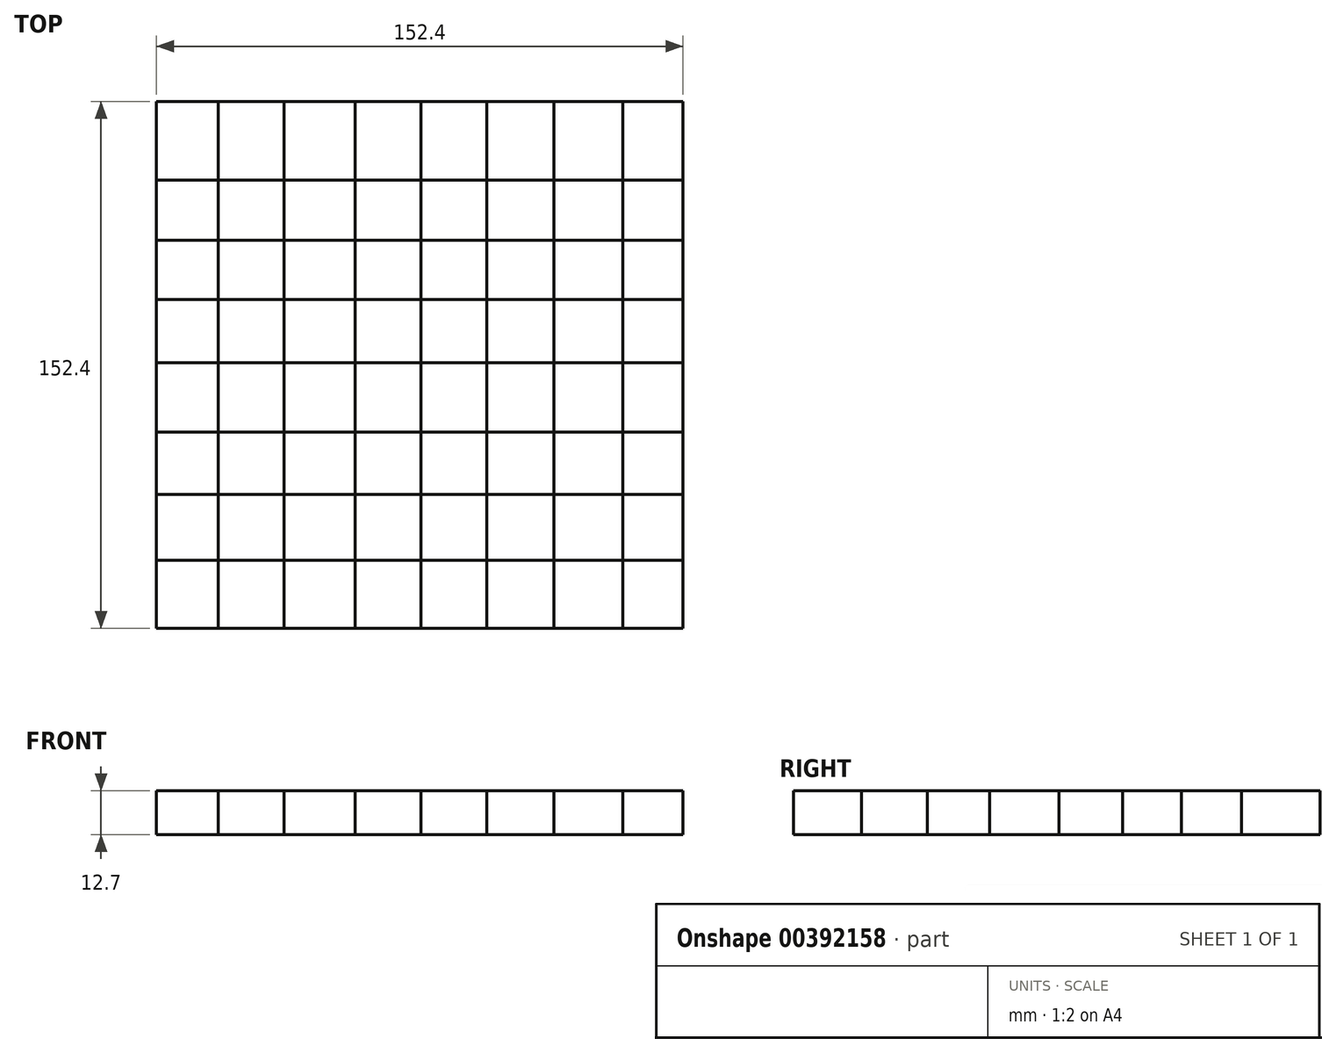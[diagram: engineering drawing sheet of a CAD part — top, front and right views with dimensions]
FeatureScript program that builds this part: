
annotation { "Feature Type Name" : "Feature", "Feature Type Description" : "" }
export const myFeature = defineFeature(function(context is Context, id is Id, definition is map)
    precondition{}
    {
        {
            var Q0;
            Q0=qCreatedBy(makeId("Top.planeOp"),FACE);
            var sketch = newSketch(context, id + "F0", { "sketchPlane" : qUnion([Q0])});
            skLineSegment(sketch, "E0.bottom", {"start": v(-76.58, 75.62) * mm, "end": v(75.82, 75.62) * mm});
            skLineSegment(sketch, "E0.top", {"start": v(-76.58, -76.78) * mm, "end": v(75.82, -76.78) * mm});
            skLineSegment(sketch, "E0.left", {"start": v(-76.58, 75.62) * mm, "end": v(-76.58, -76.78) * mm});
            skLineSegment(sketch, "E0.right", {"start": v(75.82, 75.62) * mm, "end": v(75.82, -76.78) * mm});
            skLineSegment(sketch, "E1", {"start": v(-58.72, 75.62) * mm, "end": v(-58.72, -76.78) * mm});
            skLineSegment(sketch, "E2", {"start": v(-39.68, 75.62) * mm, "end": v(-39.68, -76.78) * mm});
            skLineSegment(sketch, "E3", {"start": v(-19.03, 75.62) * mm, "end": v(-19.03, -76.78) * mm});
            skLineSegment(sketch, "E4", {"start": v(0, 75.62) * mm, "end": v(0, -76.78) * mm});
            skLineSegment(sketch, "E5", {"start": v(19.03, 75.62) * mm, "end": v(19.03, -76.78) * mm});
            skLineSegment(sketch, "E6", {"start": v(38.4, 75.62) * mm, "end": v(38.4, -76.78) * mm});
            skLineSegment(sketch, "E7", {"start": v(58.4, 75.62) * mm, "end": v(58.4, -76.78) * mm});
            skLineSegment(sketch, "E8", {"start": v(-76.58, -57.1) * mm, "end": v(75.82, -57.1) * mm});
            skLineSegment(sketch, "E9", {"start": v(-76.58, -38.07) * mm, "end": v(75.82, -38.07) * mm});
            skLineSegment(sketch, "E10", {"start": v(-76.58, -20) * mm, "end": v(75.82, -20) * mm});
            skLineSegment(sketch, "E11", {"start": v(-76.58, 0) * mm, "end": v(75.82, 0) * mm});
            skLineSegment(sketch, "E12", {"start": v(-76.58, 18.39) * mm, "end": v(75.82, 18.39) * mm});
            skLineSegment(sketch, "E13", {"start": v(-76.58, 35.49) * mm, "end": v(75.82, 35.49) * mm});
            skLineSegment(sketch, "E14", {"start": v(-76.58, 52.9) * mm, "end": v(75.82, 52.9) * mm});
            skSolve(sketch);
        }
        {
            var Q0;
            {var subQ0=sQuery(id+"F0.wireOp",EDGE,"E0.left");var subQ1=sQuery(id+"F0.wireOp",EDGE,"E0.bottom");var subQ2=makeQuery(id+"F0.imprint","INTERSECT",VERTEX,{"derivedFrom":[subQ1,subQ0]});Q0=makeQuery(id+"F0.imprint","IMPRINT",FACE,{"disambiguationData":[TD([[makeQuery(id+"F0.imprint","IMPRINT",EDGE,{"disambiguationData":[TD([[subQ2,-1.0]])],"derivedFrom":subQ1}),-1.0]])]});}
            var Q1;
            {var subQ0=sQuery(id+"F0.wireOp",EDGE,"E2");var subQ1=sQuery(id+"F0.wireOp",EDGE,"E0.bottom");var subQ2=makeQuery(id+"F0.imprint","INTERSECT",VERTEX,{"derivedFrom":[subQ1,subQ0]});Q1=makeQuery(id+"F0.imprint","IMPRINT",FACE,{"disambiguationData":[TD([[makeQuery(id+"F0.imprint","IMPRINT",EDGE,{"disambiguationData":[TD([[subQ2,-1.0]])],"derivedFrom":subQ1}),-1.0]])]});}
            var Q2;
            {var subQ0=sQuery(id+"F0.wireOp",EDGE,"E4");var subQ1=sQuery(id+"F0.wireOp",EDGE,"E0.bottom");var subQ2=makeQuery(id+"F0.imprint","INTERSECT",VERTEX,{"derivedFrom":[subQ1,subQ0]});Q2=makeQuery(id+"F0.imprint","IMPRINT",FACE,{"disambiguationData":[TD([[makeQuery(id+"F0.imprint","IMPRINT",EDGE,{"disambiguationData":[TD([[subQ2,-1.0]])],"derivedFrom":subQ1}),-1.0]])]});}
            var Q3;
            {var subQ0=sQuery(id+"F0.wireOp",EDGE,"E6");var subQ1=sQuery(id+"F0.wireOp",EDGE,"E0.bottom");var subQ2=makeQuery(id+"F0.imprint","INTERSECT",VERTEX,{"derivedFrom":[subQ1,subQ0]});Q3=makeQuery(id+"F0.imprint","IMPRINT",FACE,{"disambiguationData":[TD([[makeQuery(id+"F0.imprint","IMPRINT",EDGE,{"disambiguationData":[TD([[subQ2,-1.0]])],"derivedFrom":subQ1}),-1.0]])]});}
            var Q4;
            {var subQ0=sQuery(id+"F0.wireOp",EDGE,"E14");var subQ1=sQuery(id+"F0.wireOp",EDGE,"E1");var subQ2=makeQuery(id+"F0.imprint","INTERSECT",VERTEX,{"derivedFrom":[subQ1,subQ0]});Q4=makeQuery(id+"F0.imprint","IMPRINT",FACE,{"disambiguationData":[TD([[makeQuery(id+"F0.imprint","IMPRINT",EDGE,{"disambiguationData":[TD([[subQ2,-1.0]])],"derivedFrom":subQ1}),1.0]])]});}
            var Q5;
            {var subQ0=sQuery(id+"F0.wireOp",EDGE,"E14");var subQ1=sQuery(id+"F0.wireOp",EDGE,"E3");var subQ2=makeQuery(id+"F0.imprint","INTERSECT",VERTEX,{"derivedFrom":[subQ1,subQ0]});Q5=makeQuery(id+"F0.imprint","IMPRINT",FACE,{"disambiguationData":[TD([[makeQuery(id+"F0.imprint","IMPRINT",EDGE,{"disambiguationData":[TD([[subQ2,-1.0]])],"derivedFrom":subQ1}),1.0]])]});}
            var Q6;
            {var subQ0=sQuery(id+"F0.wireOp",EDGE,"E14");var subQ1=sQuery(id+"F0.wireOp",EDGE,"E5");var subQ2=makeQuery(id+"F0.imprint","INTERSECT",VERTEX,{"derivedFrom":[subQ1,subQ0]});Q6=makeQuery(id+"F0.imprint","IMPRINT",FACE,{"disambiguationData":[TD([[makeQuery(id+"F0.imprint","IMPRINT",EDGE,{"disambiguationData":[TD([[subQ2,-1.0]])],"derivedFrom":subQ1}),1.0]])]});}
            var Q7;
            {var subQ0=sQuery(id+"F0.wireOp",EDGE,"E13");var subQ1=sQuery(id+"F0.wireOp",EDGE,"E0.right");var subQ2=makeQuery(id+"F0.imprint","INTERSECT",VERTEX,{"derivedFrom":[subQ1,subQ0]});Q7=makeQuery(id+"F0.imprint","IMPRINT",FACE,{"disambiguationData":[TD([[makeQuery(id+"F0.imprint","IMPRINT",EDGE,{"disambiguationData":[TD([[subQ2,1.0]])],"derivedFrom":subQ1}),-1.0]])]});}
            var Q8;
            {var subQ0=sQuery(id+"F0.wireOp",EDGE,"E13");var subQ1=sQuery(id+"F0.wireOp",EDGE,"E6");var subQ2=makeQuery(id+"F0.imprint","INTERSECT",VERTEX,{"derivedFrom":[subQ1,subQ0]});Q8=makeQuery(id+"F0.imprint","IMPRINT",FACE,{"disambiguationData":[TD([[makeQuery(id+"F0.imprint","IMPRINT",EDGE,{"disambiguationData":[TD([[subQ2,-1.0]])],"derivedFrom":subQ1}),1.0]])]});}
            var Q9;
            {var subQ0=sQuery(id+"F0.wireOp",EDGE,"E13");var subQ1=sQuery(id+"F0.wireOp",EDGE,"E4");var subQ2=makeQuery(id+"F0.imprint","INTERSECT",VERTEX,{"derivedFrom":[subQ1,subQ0]});Q9=makeQuery(id+"F0.imprint","IMPRINT",FACE,{"disambiguationData":[TD([[makeQuery(id+"F0.imprint","IMPRINT",EDGE,{"disambiguationData":[TD([[subQ2,-1.0]])],"derivedFrom":subQ1}),1.0]])]});}
            var Q10;
            {var subQ0=sQuery(id+"F0.wireOp",EDGE,"E13");var subQ1=sQuery(id+"F0.wireOp",EDGE,"E2");var subQ2=makeQuery(id+"F0.imprint","INTERSECT",VERTEX,{"derivedFrom":[subQ1,subQ0]});Q10=makeQuery(id+"F0.imprint","IMPRINT",FACE,{"disambiguationData":[TD([[makeQuery(id+"F0.imprint","IMPRINT",EDGE,{"disambiguationData":[TD([[subQ2,-1.0]])],"derivedFrom":subQ1}),1.0]])]});}
            var Q11;
            {var subQ0=sQuery(id+"F0.wireOp",EDGE,"E12");var subQ1=sQuery(id+"F0.wireOp",EDGE,"E0.left");var subQ2=makeQuery(id+"F0.imprint","INTERSECT",VERTEX,{"derivedFrom":[subQ1,subQ0]});Q11=makeQuery(id+"F0.imprint","IMPRINT",FACE,{"disambiguationData":[TD([[makeQuery(id+"F0.imprint","IMPRINT",EDGE,{"disambiguationData":[TD([[subQ2,1.0]])],"derivedFrom":subQ1}),1.0]])]});}
            var Q12;
            {var subQ0=sQuery(id+"F0.wireOp",EDGE,"E12");var subQ1=sQuery(id+"F0.wireOp",EDGE,"E1");var subQ2=makeQuery(id+"F0.imprint","INTERSECT",VERTEX,{"derivedFrom":[subQ1,subQ0]});Q12=makeQuery(id+"F0.imprint","IMPRINT",FACE,{"disambiguationData":[TD([[makeQuery(id+"F0.imprint","IMPRINT",EDGE,{"disambiguationData":[TD([[subQ2,-1.0]])],"derivedFrom":subQ1}),1.0]])]});}
            var Q13;
            {var subQ0=sQuery(id+"F0.wireOp",EDGE,"E12");var subQ1=sQuery(id+"F0.wireOp",EDGE,"E3");var subQ2=makeQuery(id+"F0.imprint","INTERSECT",VERTEX,{"derivedFrom":[subQ1,subQ0]});Q13=makeQuery(id+"F0.imprint","IMPRINT",FACE,{"disambiguationData":[TD([[makeQuery(id+"F0.imprint","IMPRINT",EDGE,{"disambiguationData":[TD([[subQ2,-1.0]])],"derivedFrom":subQ1}),1.0]])]});}
            var Q14;
            {var subQ0=sQuery(id+"F0.wireOp",EDGE,"E12");var subQ1=sQuery(id+"F0.wireOp",EDGE,"E5");var subQ2=makeQuery(id+"F0.imprint","INTERSECT",VERTEX,{"derivedFrom":[subQ1,subQ0]});Q14=makeQuery(id+"F0.imprint","IMPRINT",FACE,{"disambiguationData":[TD([[makeQuery(id+"F0.imprint","IMPRINT",EDGE,{"disambiguationData":[TD([[subQ2,-1.0]])],"derivedFrom":subQ1}),1.0]])]});}
            var Q15;
            {var subQ0=sQuery(id+"F0.wireOp",EDGE,"E11");var subQ1=sQuery(id+"F0.wireOp",EDGE,"E0.right");var subQ2=makeQuery(id+"F0.imprint","INTERSECT",VERTEX,{"derivedFrom":[subQ1,subQ0]});Q15=makeQuery(id+"F0.imprint","IMPRINT",FACE,{"disambiguationData":[TD([[makeQuery(id+"F0.imprint","IMPRINT",EDGE,{"disambiguationData":[TD([[subQ2,1.0]])],"derivedFrom":subQ1}),-1.0]])]});}
            var Q16;
            {var subQ0=sQuery(id+"F0.wireOp",EDGE,"E11");var subQ1=sQuery(id+"F0.wireOp",EDGE,"E6");var subQ2=makeQuery(id+"F0.imprint","INTERSECT",VERTEX,{"derivedFrom":[subQ1,subQ0]});Q16=makeQuery(id+"F0.imprint","IMPRINT",FACE,{"disambiguationData":[TD([[makeQuery(id+"F0.imprint","IMPRINT",EDGE,{"disambiguationData":[TD([[subQ2,-1.0]])],"derivedFrom":subQ1}),1.0]])]});}
            var Q17;
            {var subQ0=sQuery(id+"F0.wireOp",EDGE,"E11");var subQ1=sQuery(id+"F0.wireOp",EDGE,"E4");var subQ2=makeQuery(id+"F0.imprint","INTERSECT",VERTEX,{"derivedFrom":[subQ1,subQ0]});Q17=makeQuery(id+"F0.imprint","IMPRINT",FACE,{"disambiguationData":[TD([[makeQuery(id+"F0.imprint","IMPRINT",EDGE,{"disambiguationData":[TD([[subQ2,-1.0]])],"derivedFrom":subQ1}),1.0]])]});}
            var Q18;
            {var subQ0=sQuery(id+"F0.wireOp",EDGE,"E11");var subQ1=sQuery(id+"F0.wireOp",EDGE,"E2");var subQ2=makeQuery(id+"F0.imprint","INTERSECT",VERTEX,{"derivedFrom":[subQ1,subQ0]});Q18=makeQuery(id+"F0.imprint","IMPRINT",FACE,{"disambiguationData":[TD([[makeQuery(id+"F0.imprint","IMPRINT",EDGE,{"disambiguationData":[TD([[subQ2,-1.0]])],"derivedFrom":subQ1}),1.0]])]});}
            var Q19;
            {var subQ0=sQuery(id+"F0.wireOp",EDGE,"E10");var subQ1=sQuery(id+"F0.wireOp",EDGE,"E0.left");var subQ2=makeQuery(id+"F0.imprint","INTERSECT",VERTEX,{"derivedFrom":[subQ1,subQ0]});Q19=makeQuery(id+"F0.imprint","IMPRINT",FACE,{"disambiguationData":[TD([[makeQuery(id+"F0.imprint","IMPRINT",EDGE,{"disambiguationData":[TD([[subQ2,1.0]])],"derivedFrom":subQ1}),1.0]])]});}
            var Q20;
            {var subQ0=sQuery(id+"F0.wireOp",EDGE,"E10");var subQ1=sQuery(id+"F0.wireOp",EDGE,"E1");var subQ2=makeQuery(id+"F0.imprint","INTERSECT",VERTEX,{"derivedFrom":[subQ1,subQ0]});Q20=makeQuery(id+"F0.imprint","IMPRINT",FACE,{"disambiguationData":[TD([[makeQuery(id+"F0.imprint","IMPRINT",EDGE,{"disambiguationData":[TD([[subQ2,-1.0]])],"derivedFrom":subQ1}),1.0]])]});}
            var Q21;
            {var subQ0=sQuery(id+"F0.wireOp",EDGE,"E10");var subQ1=sQuery(id+"F0.wireOp",EDGE,"E3");var subQ2=makeQuery(id+"F0.imprint","INTERSECT",VERTEX,{"derivedFrom":[subQ1,subQ0]});Q21=makeQuery(id+"F0.imprint","IMPRINT",FACE,{"disambiguationData":[TD([[makeQuery(id+"F0.imprint","IMPRINT",EDGE,{"disambiguationData":[TD([[subQ2,-1.0]])],"derivedFrom":subQ1}),1.0]])]});}
            var Q22;
            {var subQ0=sQuery(id+"F0.wireOp",EDGE,"E10");var subQ1=sQuery(id+"F0.wireOp",EDGE,"E5");var subQ2=makeQuery(id+"F0.imprint","INTERSECT",VERTEX,{"derivedFrom":[subQ1,subQ0]});Q22=makeQuery(id+"F0.imprint","IMPRINT",FACE,{"disambiguationData":[TD([[makeQuery(id+"F0.imprint","IMPRINT",EDGE,{"disambiguationData":[TD([[subQ2,-1.0]])],"derivedFrom":subQ1}),1.0]])]});}
            var Q23;
            {var subQ0=sQuery(id+"F0.wireOp",EDGE,"E9");var subQ1=sQuery(id+"F0.wireOp",EDGE,"E0.right");var subQ2=makeQuery(id+"F0.imprint","INTERSECT",VERTEX,{"derivedFrom":[subQ1,subQ0]});Q23=makeQuery(id+"F0.imprint","IMPRINT",FACE,{"disambiguationData":[TD([[makeQuery(id+"F0.imprint","IMPRINT",EDGE,{"disambiguationData":[TD([[subQ2,1.0]])],"derivedFrom":subQ1}),-1.0]])]});}
            var Q24;
            {var subQ0=sQuery(id+"F0.wireOp",EDGE,"E9");var subQ1=sQuery(id+"F0.wireOp",EDGE,"E6");var subQ2=makeQuery(id+"F0.imprint","INTERSECT",VERTEX,{"derivedFrom":[subQ1,subQ0]});Q24=makeQuery(id+"F0.imprint","IMPRINT",FACE,{"disambiguationData":[TD([[makeQuery(id+"F0.imprint","IMPRINT",EDGE,{"disambiguationData":[TD([[subQ2,-1.0]])],"derivedFrom":subQ1}),1.0]])]});}
            var Q25;
            {var subQ0=sQuery(id+"F0.wireOp",EDGE,"E9");var subQ1=sQuery(id+"F0.wireOp",EDGE,"E4");var subQ2=makeQuery(id+"F0.imprint","INTERSECT",VERTEX,{"derivedFrom":[subQ1,subQ0]});Q25=makeQuery(id+"F0.imprint","IMPRINT",FACE,{"disambiguationData":[TD([[makeQuery(id+"F0.imprint","IMPRINT",EDGE,{"disambiguationData":[TD([[subQ2,-1.0]])],"derivedFrom":subQ1}),1.0]])]});}
            var Q26;
            {var subQ0=sQuery(id+"F0.wireOp",EDGE,"E9");var subQ1=sQuery(id+"F0.wireOp",EDGE,"E2");var subQ2=makeQuery(id+"F0.imprint","INTERSECT",VERTEX,{"derivedFrom":[subQ1,subQ0]});Q26=makeQuery(id+"F0.imprint","IMPRINT",FACE,{"disambiguationData":[TD([[makeQuery(id+"F0.imprint","IMPRINT",EDGE,{"disambiguationData":[TD([[subQ2,-1.0]])],"derivedFrom":subQ1}),1.0]])]});}
            var Q27;
            {var subQ0=sQuery(id+"F0.wireOp",EDGE,"E8");var subQ1=sQuery(id+"F0.wireOp",EDGE,"E0.left");var subQ2=makeQuery(id+"F0.imprint","INTERSECT",VERTEX,{"derivedFrom":[subQ1,subQ0]});Q27=makeQuery(id+"F0.imprint","IMPRINT",FACE,{"disambiguationData":[TD([[makeQuery(id+"F0.imprint","IMPRINT",EDGE,{"disambiguationData":[TD([[subQ2,1.0]])],"derivedFrom":subQ1}),1.0]])]});}
            var Q28;
            {var subQ0=sQuery(id+"F0.wireOp",EDGE,"E1");var subQ1=sQuery(id+"F0.wireOp",EDGE,"E0.top");var subQ2=makeQuery(id+"F0.imprint","INTERSECT",VERTEX,{"derivedFrom":[subQ1,subQ0]});Q28=makeQuery(id+"F0.imprint","IMPRINT",FACE,{"disambiguationData":[TD([[makeQuery(id+"F0.imprint","IMPRINT",EDGE,{"disambiguationData":[TD([[subQ2,-1.0]])],"derivedFrom":subQ1}),1.0]])]});}
            var Q29;
            {var subQ0=sQuery(id+"F0.wireOp",EDGE,"E3");var subQ1=sQuery(id+"F0.wireOp",EDGE,"E0.top");var subQ2=makeQuery(id+"F0.imprint","INTERSECT",VERTEX,{"derivedFrom":[subQ1,subQ0]});Q29=makeQuery(id+"F0.imprint","IMPRINT",FACE,{"disambiguationData":[TD([[makeQuery(id+"F0.imprint","IMPRINT",EDGE,{"disambiguationData":[TD([[subQ2,-1.0]])],"derivedFrom":subQ1}),1.0]])]});}
            var Q30;
            {var subQ0=sQuery(id+"F0.wireOp",EDGE,"E5");var subQ1=sQuery(id+"F0.wireOp",EDGE,"E0.top");var subQ2=makeQuery(id+"F0.imprint","INTERSECT",VERTEX,{"derivedFrom":[subQ1,subQ0]});Q30=makeQuery(id+"F0.imprint","IMPRINT",FACE,{"disambiguationData":[TD([[makeQuery(id+"F0.imprint","IMPRINT",EDGE,{"disambiguationData":[TD([[subQ2,-1.0]])],"derivedFrom":subQ1}),1.0]])]});}
            var Q31;
            {var subQ0=sQuery(id+"F0.wireOp",EDGE,"E0.right");var subQ1=sQuery(id+"F0.wireOp",EDGE,"E0.top");var subQ2=makeQuery(id+"F0.imprint","INTERSECT",VERTEX,{"derivedFrom":[subQ1,subQ0]});Q31=makeQuery(id+"F0.imprint","IMPRINT",FACE,{"disambiguationData":[TD([[makeQuery(id+"F0.imprint","IMPRINT",EDGE,{"disambiguationData":[TD([[subQ2,1.0]])],"derivedFrom":subQ1}),1.0]])]});}
            extrude(context, id + "F1", {"entities" : qUnion([Q0, Q1, Q2, Q3, Q4, Q5, Q6, Q7, Q8, Q9, Q10, Q11, Q12, Q13, Q14, Q15, Q16, Q17, Q18, Q19, Q20, Q21, Q22, Q23, Q24, Q25, Q26, Q27, Q28, Q29, Q30, Q31]), "depth" : 12.7 * mm});
        }
        {
            var Q0;
            {var subQ0=sQuery(id+"F0.wireOp",EDGE,"E1");var subQ1=sQuery(id+"F0.wireOp",EDGE,"E0.bottom");var subQ2=makeQuery(id+"F0.imprint","INTERSECT",VERTEX,{"derivedFrom":[subQ1,subQ0]});Q0=makeQuery(id+"F0.imprint","IMPRINT",FACE,{"disambiguationData":[TD([[makeQuery(id+"F0.imprint","IMPRINT",EDGE,{"disambiguationData":[TD([[subQ2,-1.0]])],"derivedFrom":subQ1}),-1.0]])]});}
            var Q1;
            {var subQ0=sQuery(id+"F0.wireOp",EDGE,"E3");var subQ1=sQuery(id+"F0.wireOp",EDGE,"E0.bottom");var subQ2=makeQuery(id+"F0.imprint","INTERSECT",VERTEX,{"derivedFrom":[subQ1,subQ0]});Q1=makeQuery(id+"F0.imprint","IMPRINT",FACE,{"disambiguationData":[TD([[makeQuery(id+"F0.imprint","IMPRINT",EDGE,{"disambiguationData":[TD([[subQ2,-1.0]])],"derivedFrom":subQ1}),-1.0]])]});}
            var Q2;
            {var subQ0=sQuery(id+"F0.wireOp",EDGE,"E5");var subQ1=sQuery(id+"F0.wireOp",EDGE,"E0.bottom");var subQ2=makeQuery(id+"F0.imprint","INTERSECT",VERTEX,{"derivedFrom":[subQ1,subQ0]});Q2=makeQuery(id+"F0.imprint","IMPRINT",FACE,{"disambiguationData":[TD([[makeQuery(id+"F0.imprint","IMPRINT",EDGE,{"disambiguationData":[TD([[subQ2,-1.0]])],"derivedFrom":subQ1}),-1.0]])]});}
            var Q3;
            {var subQ0=sQuery(id+"F0.wireOp",EDGE,"E0.right");var subQ1=sQuery(id+"F0.wireOp",EDGE,"E0.bottom");var subQ2=makeQuery(id+"F0.imprint","INTERSECT",VERTEX,{"derivedFrom":[subQ1,subQ0]});Q3=makeQuery(id+"F0.imprint","IMPRINT",FACE,{"disambiguationData":[TD([[makeQuery(id+"F0.imprint","IMPRINT",EDGE,{"disambiguationData":[TD([[subQ2,1.0]])],"derivedFrom":subQ1}),-1.0]])]});}
            var Q4;
            {var subQ0=sQuery(id+"F0.wireOp",EDGE,"E13");var subQ1=sQuery(id+"F0.wireOp",EDGE,"E0.left");var subQ2=makeQuery(id+"F0.imprint","INTERSECT",VERTEX,{"derivedFrom":[subQ1,subQ0]});Q4=makeQuery(id+"F0.imprint","IMPRINT",FACE,{"disambiguationData":[TD([[makeQuery(id+"F0.imprint","IMPRINT",EDGE,{"disambiguationData":[TD([[subQ2,1.0]])],"derivedFrom":subQ1}),1.0]])]});}
            var Q5;
            {var subQ0=sQuery(id+"F0.wireOp",EDGE,"E14");var subQ1=sQuery(id+"F0.wireOp",EDGE,"E2");var subQ2=makeQuery(id+"F0.imprint","INTERSECT",VERTEX,{"derivedFrom":[subQ1,subQ0]});Q5=makeQuery(id+"F0.imprint","IMPRINT",FACE,{"disambiguationData":[TD([[makeQuery(id+"F0.imprint","IMPRINT",EDGE,{"disambiguationData":[TD([[subQ2,-1.0]])],"derivedFrom":subQ1}),1.0]])]});}
            var Q6;
            {var subQ0=sQuery(id+"F0.wireOp",EDGE,"E14");var subQ1=sQuery(id+"F0.wireOp",EDGE,"E4");var subQ2=makeQuery(id+"F0.imprint","INTERSECT",VERTEX,{"derivedFrom":[subQ1,subQ0]});Q6=makeQuery(id+"F0.imprint","IMPRINT",FACE,{"disambiguationData":[TD([[makeQuery(id+"F0.imprint","IMPRINT",EDGE,{"disambiguationData":[TD([[subQ2,-1.0]])],"derivedFrom":subQ1}),1.0]])]});}
            var Q7;
            {var subQ0=sQuery(id+"F0.wireOp",EDGE,"E14");var subQ1=sQuery(id+"F0.wireOp",EDGE,"E6");var subQ2=makeQuery(id+"F0.imprint","INTERSECT",VERTEX,{"derivedFrom":[subQ1,subQ0]});Q7=makeQuery(id+"F0.imprint","IMPRINT",FACE,{"disambiguationData":[TD([[makeQuery(id+"F0.imprint","IMPRINT",EDGE,{"disambiguationData":[TD([[subQ2,-1.0]])],"derivedFrom":subQ1}),1.0]])]});}
            var Q8;
            {var subQ0=sQuery(id+"F0.wireOp",EDGE,"E12");var subQ1=sQuery(id+"F0.wireOp",EDGE,"E0.right");var subQ2=makeQuery(id+"F0.imprint","INTERSECT",VERTEX,{"derivedFrom":[subQ1,subQ0]});Q8=makeQuery(id+"F0.imprint","IMPRINT",FACE,{"disambiguationData":[TD([[makeQuery(id+"F0.imprint","IMPRINT",EDGE,{"disambiguationData":[TD([[subQ2,1.0]])],"derivedFrom":subQ1}),-1.0]])]});}
            var Q9;
            {var subQ0=sQuery(id+"F0.wireOp",EDGE,"E13");var subQ1=sQuery(id+"F0.wireOp",EDGE,"E5");var subQ2=makeQuery(id+"F0.imprint","INTERSECT",VERTEX,{"derivedFrom":[subQ1,subQ0]});Q9=makeQuery(id+"F0.imprint","IMPRINT",FACE,{"disambiguationData":[TD([[makeQuery(id+"F0.imprint","IMPRINT",EDGE,{"disambiguationData":[TD([[subQ2,-1.0]])],"derivedFrom":subQ1}),1.0]])]});}
            var Q10;
            {var subQ0=sQuery(id+"F0.wireOp",EDGE,"E13");var subQ1=sQuery(id+"F0.wireOp",EDGE,"E3");var subQ2=makeQuery(id+"F0.imprint","INTERSECT",VERTEX,{"derivedFrom":[subQ1,subQ0]});Q10=makeQuery(id+"F0.imprint","IMPRINT",FACE,{"disambiguationData":[TD([[makeQuery(id+"F0.imprint","IMPRINT",EDGE,{"disambiguationData":[TD([[subQ2,-1.0]])],"derivedFrom":subQ1}),1.0]])]});}
            var Q11;
            {var subQ0=sQuery(id+"F0.wireOp",EDGE,"E13");var subQ1=sQuery(id+"F0.wireOp",EDGE,"E1");var subQ2=makeQuery(id+"F0.imprint","INTERSECT",VERTEX,{"derivedFrom":[subQ1,subQ0]});Q11=makeQuery(id+"F0.imprint","IMPRINT",FACE,{"disambiguationData":[TD([[makeQuery(id+"F0.imprint","IMPRINT",EDGE,{"disambiguationData":[TD([[subQ2,-1.0]])],"derivedFrom":subQ1}),1.0]])]});}
            var Q12;
            {var subQ0=sQuery(id+"F0.wireOp",EDGE,"E11");var subQ1=sQuery(id+"F0.wireOp",EDGE,"E0.left");var subQ2=makeQuery(id+"F0.imprint","INTERSECT",VERTEX,{"derivedFrom":[subQ1,subQ0]});Q12=makeQuery(id+"F0.imprint","IMPRINT",FACE,{"disambiguationData":[TD([[makeQuery(id+"F0.imprint","IMPRINT",EDGE,{"disambiguationData":[TD([[subQ2,1.0]])],"derivedFrom":subQ1}),1.0]])]});}
            var Q13;
            {var subQ0=sQuery(id+"F0.wireOp",EDGE,"E12");var subQ1=sQuery(id+"F0.wireOp",EDGE,"E2");var subQ2=makeQuery(id+"F0.imprint","INTERSECT",VERTEX,{"derivedFrom":[subQ1,subQ0]});Q13=makeQuery(id+"F0.imprint","IMPRINT",FACE,{"disambiguationData":[TD([[makeQuery(id+"F0.imprint","IMPRINT",EDGE,{"disambiguationData":[TD([[subQ2,-1.0]])],"derivedFrom":subQ1}),1.0]])]});}
            var Q14;
            {var subQ0=sQuery(id+"F0.wireOp",EDGE,"E12");var subQ1=sQuery(id+"F0.wireOp",EDGE,"E4");var subQ2=makeQuery(id+"F0.imprint","INTERSECT",VERTEX,{"derivedFrom":[subQ1,subQ0]});Q14=makeQuery(id+"F0.imprint","IMPRINT",FACE,{"disambiguationData":[TD([[makeQuery(id+"F0.imprint","IMPRINT",EDGE,{"disambiguationData":[TD([[subQ2,-1.0]])],"derivedFrom":subQ1}),1.0]])]});}
            var Q15;
            {var subQ0=sQuery(id+"F0.wireOp",EDGE,"E12");var subQ1=sQuery(id+"F0.wireOp",EDGE,"E6");var subQ2=makeQuery(id+"F0.imprint","INTERSECT",VERTEX,{"derivedFrom":[subQ1,subQ0]});Q15=makeQuery(id+"F0.imprint","IMPRINT",FACE,{"disambiguationData":[TD([[makeQuery(id+"F0.imprint","IMPRINT",EDGE,{"disambiguationData":[TD([[subQ2,-1.0]])],"derivedFrom":subQ1}),1.0]])]});}
            var Q16;
            {var subQ0=sQuery(id+"F0.wireOp",EDGE,"E10");var subQ1=sQuery(id+"F0.wireOp",EDGE,"E0.right");var subQ2=makeQuery(id+"F0.imprint","INTERSECT",VERTEX,{"derivedFrom":[subQ1,subQ0]});Q16=makeQuery(id+"F0.imprint","IMPRINT",FACE,{"disambiguationData":[TD([[makeQuery(id+"F0.imprint","IMPRINT",EDGE,{"disambiguationData":[TD([[subQ2,1.0]])],"derivedFrom":subQ1}),-1.0]])]});}
            var Q17;
            {var subQ0=sQuery(id+"F0.wireOp",EDGE,"E11");var subQ1=sQuery(id+"F0.wireOp",EDGE,"E5");var subQ2=makeQuery(id+"F0.imprint","INTERSECT",VERTEX,{"derivedFrom":[subQ1,subQ0]});Q17=makeQuery(id+"F0.imprint","IMPRINT",FACE,{"disambiguationData":[TD([[makeQuery(id+"F0.imprint","IMPRINT",EDGE,{"disambiguationData":[TD([[subQ2,-1.0]])],"derivedFrom":subQ1}),1.0]])]});}
            var Q18;
            {var subQ0=sQuery(id+"F0.wireOp",EDGE,"E11");var subQ1=sQuery(id+"F0.wireOp",EDGE,"E3");var subQ2=makeQuery(id+"F0.imprint","INTERSECT",VERTEX,{"derivedFrom":[subQ1,subQ0]});Q18=makeQuery(id+"F0.imprint","IMPRINT",FACE,{"disambiguationData":[TD([[makeQuery(id+"F0.imprint","IMPRINT",EDGE,{"disambiguationData":[TD([[subQ2,-1.0]])],"derivedFrom":subQ1}),1.0]])]});}
            var Q19;
            {var subQ0=sQuery(id+"F0.wireOp",EDGE,"E11");var subQ1=sQuery(id+"F0.wireOp",EDGE,"E1");var subQ2=makeQuery(id+"F0.imprint","INTERSECT",VERTEX,{"derivedFrom":[subQ1,subQ0]});Q19=makeQuery(id+"F0.imprint","IMPRINT",FACE,{"disambiguationData":[TD([[makeQuery(id+"F0.imprint","IMPRINT",EDGE,{"disambiguationData":[TD([[subQ2,-1.0]])],"derivedFrom":subQ1}),1.0]])]});}
            var Q20;
            {var subQ0=sQuery(id+"F0.wireOp",EDGE,"E9");var subQ1=sQuery(id+"F0.wireOp",EDGE,"E0.left");var subQ2=makeQuery(id+"F0.imprint","INTERSECT",VERTEX,{"derivedFrom":[subQ1,subQ0]});Q20=makeQuery(id+"F0.imprint","IMPRINT",FACE,{"disambiguationData":[TD([[makeQuery(id+"F0.imprint","IMPRINT",EDGE,{"disambiguationData":[TD([[subQ2,1.0]])],"derivedFrom":subQ1}),1.0]])]});}
            var Q21;
            {var subQ0=sQuery(id+"F0.wireOp",EDGE,"E10");var subQ1=sQuery(id+"F0.wireOp",EDGE,"E2");var subQ2=makeQuery(id+"F0.imprint","INTERSECT",VERTEX,{"derivedFrom":[subQ1,subQ0]});Q21=makeQuery(id+"F0.imprint","IMPRINT",FACE,{"disambiguationData":[TD([[makeQuery(id+"F0.imprint","IMPRINT",EDGE,{"disambiguationData":[TD([[subQ2,-1.0]])],"derivedFrom":subQ1}),1.0]])]});}
            var Q22;
            {var subQ0=sQuery(id+"F0.wireOp",EDGE,"E10");var subQ1=sQuery(id+"F0.wireOp",EDGE,"E4");var subQ2=makeQuery(id+"F0.imprint","INTERSECT",VERTEX,{"derivedFrom":[subQ1,subQ0]});Q22=makeQuery(id+"F0.imprint","IMPRINT",FACE,{"disambiguationData":[TD([[makeQuery(id+"F0.imprint","IMPRINT",EDGE,{"disambiguationData":[TD([[subQ2,-1.0]])],"derivedFrom":subQ1}),1.0]])]});}
            var Q23;
            {var subQ0=sQuery(id+"F0.wireOp",EDGE,"E10");var subQ1=sQuery(id+"F0.wireOp",EDGE,"E6");var subQ2=makeQuery(id+"F0.imprint","INTERSECT",VERTEX,{"derivedFrom":[subQ1,subQ0]});Q23=makeQuery(id+"F0.imprint","IMPRINT",FACE,{"disambiguationData":[TD([[makeQuery(id+"F0.imprint","IMPRINT",EDGE,{"disambiguationData":[TD([[subQ2,-1.0]])],"derivedFrom":subQ1}),1.0]])]});}
            var Q24;
            {var subQ0=sQuery(id+"F0.wireOp",EDGE,"E8");var subQ1=sQuery(id+"F0.wireOp",EDGE,"E0.right");var subQ2=makeQuery(id+"F0.imprint","INTERSECT",VERTEX,{"derivedFrom":[subQ1,subQ0]});Q24=makeQuery(id+"F0.imprint","IMPRINT",FACE,{"disambiguationData":[TD([[makeQuery(id+"F0.imprint","IMPRINT",EDGE,{"disambiguationData":[TD([[subQ2,1.0]])],"derivedFrom":subQ1}),-1.0]])]});}
            var Q25;
            {var subQ0=sQuery(id+"F0.wireOp",EDGE,"E9");var subQ1=sQuery(id+"F0.wireOp",EDGE,"E5");var subQ2=makeQuery(id+"F0.imprint","INTERSECT",VERTEX,{"derivedFrom":[subQ1,subQ0]});Q25=makeQuery(id+"F0.imprint","IMPRINT",FACE,{"disambiguationData":[TD([[makeQuery(id+"F0.imprint","IMPRINT",EDGE,{"disambiguationData":[TD([[subQ2,-1.0]])],"derivedFrom":subQ1}),1.0]])]});}
            var Q26;
            {var subQ0=sQuery(id+"F0.wireOp",EDGE,"E9");var subQ1=sQuery(id+"F0.wireOp",EDGE,"E3");var subQ2=makeQuery(id+"F0.imprint","INTERSECT",VERTEX,{"derivedFrom":[subQ1,subQ0]});Q26=makeQuery(id+"F0.imprint","IMPRINT",FACE,{"disambiguationData":[TD([[makeQuery(id+"F0.imprint","IMPRINT",EDGE,{"disambiguationData":[TD([[subQ2,-1.0]])],"derivedFrom":subQ1}),1.0]])]});}
            var Q27;
            {var subQ0=sQuery(id+"F0.wireOp",EDGE,"E9");var subQ1=sQuery(id+"F0.wireOp",EDGE,"E1");var subQ2=makeQuery(id+"F0.imprint","INTERSECT",VERTEX,{"derivedFrom":[subQ1,subQ0]});Q27=makeQuery(id+"F0.imprint","IMPRINT",FACE,{"disambiguationData":[TD([[makeQuery(id+"F0.imprint","IMPRINT",EDGE,{"disambiguationData":[TD([[subQ2,-1.0]])],"derivedFrom":subQ1}),1.0]])]});}
            var Q28;
            {var subQ0=sQuery(id+"F0.wireOp",EDGE,"E0.left");var subQ1=sQuery(id+"F0.wireOp",EDGE,"E0.top");var subQ2=makeQuery(id+"F0.imprint","INTERSECT",VERTEX,{"derivedFrom":[subQ1,subQ0]});Q28=makeQuery(id+"F0.imprint","IMPRINT",FACE,{"disambiguationData":[TD([[makeQuery(id+"F0.imprint","IMPRINT",EDGE,{"disambiguationData":[TD([[subQ2,-1.0]])],"derivedFrom":subQ1}),1.0]])]});}
            var Q29;
            {var subQ0=sQuery(id+"F0.wireOp",EDGE,"E2");var subQ1=sQuery(id+"F0.wireOp",EDGE,"E0.top");var subQ2=makeQuery(id+"F0.imprint","INTERSECT",VERTEX,{"derivedFrom":[subQ1,subQ0]});Q29=makeQuery(id+"F0.imprint","IMPRINT",FACE,{"disambiguationData":[TD([[makeQuery(id+"F0.imprint","IMPRINT",EDGE,{"disambiguationData":[TD([[subQ2,-1.0]])],"derivedFrom":subQ1}),1.0]])]});}
            var Q30;
            {var subQ0=sQuery(id+"F0.wireOp",EDGE,"E4");var subQ1=sQuery(id+"F0.wireOp",EDGE,"E0.top");var subQ2=makeQuery(id+"F0.imprint","INTERSECT",VERTEX,{"derivedFrom":[subQ1,subQ0]});Q30=makeQuery(id+"F0.imprint","IMPRINT",FACE,{"disambiguationData":[TD([[makeQuery(id+"F0.imprint","IMPRINT",EDGE,{"disambiguationData":[TD([[subQ2,-1.0]])],"derivedFrom":subQ1}),1.0]])]});}
            var Q31;
            {var subQ0=sQuery(id+"F0.wireOp",EDGE,"E6");var subQ1=sQuery(id+"F0.wireOp",EDGE,"E0.top");var subQ2=makeQuery(id+"F0.imprint","INTERSECT",VERTEX,{"derivedFrom":[subQ1,subQ0]});Q31=makeQuery(id+"F0.imprint","IMPRINT",FACE,{"disambiguationData":[TD([[makeQuery(id+"F0.imprint","IMPRINT",EDGE,{"disambiguationData":[TD([[subQ2,-1.0]])],"derivedFrom":subQ1}),1.0]])]});}
            extrude(context, id + "F2", {"entities" : qUnion([Q0, Q1, Q2, Q3, Q4, Q5, Q6, Q7, Q8, Q9, Q10, Q11, Q12, Q13, Q14, Q15, Q16, Q17, Q18, Q19, Q20, Q21, Q22, Q23, Q24, Q25, Q26, Q27, Q28, Q29, Q30, Q31]), "depth" : 12.7 * mm});
        }
    });
